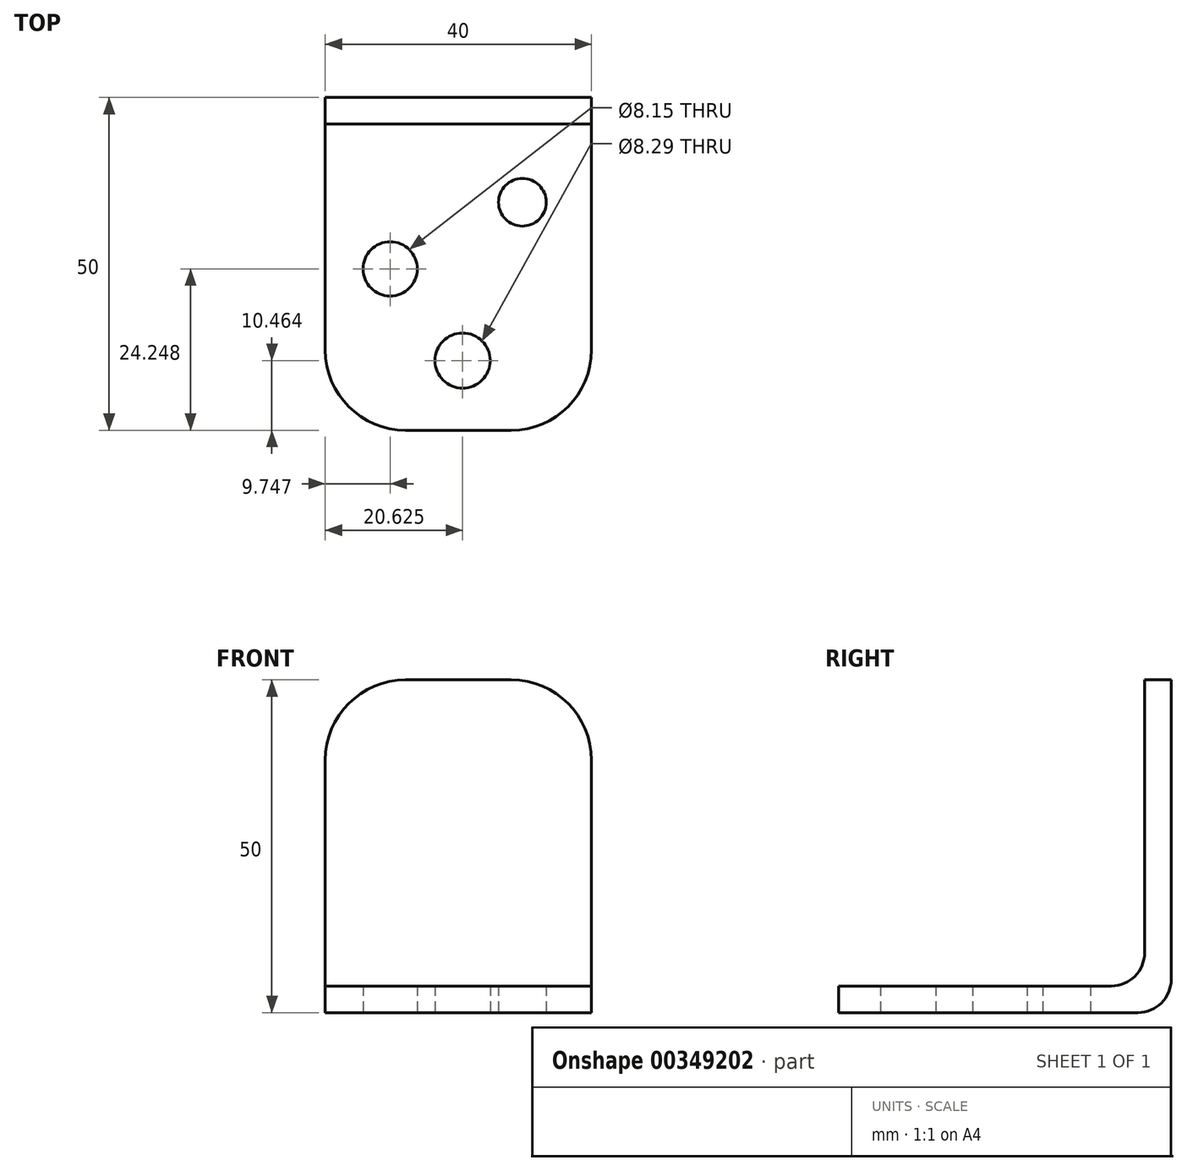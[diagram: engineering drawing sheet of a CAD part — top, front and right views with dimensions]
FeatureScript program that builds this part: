
annotation { "Feature Type Name" : "Feature", "Feature Type Description" : "" }
export const myFeature = defineFeature(function(context is Context, id is Id, definition is map)
    precondition{}
    {
        {
            var Q0;
            Q0=qCreatedBy(makeId("Front.planeOp"),FACE);
            var sketch = newSketch(context, id + "F0", { "sketchPlane" : qUnion([Q0])});
            skLineSegment(sketch, "E0.bottom", {"start": v(0, 0) * mm, "end": v(40, 0) * mm});
            skLineSegment(sketch, "E0.top", {"start": v(0, 50) * mm, "end": v(40, 50) * mm});
            skLineSegment(sketch, "E0.left", {"start": v(0, 0) * mm, "end": v(0, 50) * mm});
            skLineSegment(sketch, "E0.right", {"start": v(40, 0) * mm, "end": v(40, 50) * mm});
            skSolve(sketch);
        }
        {
            var Q0;
            Q0=makeQuery(id+"F0.imprint","IMPRINT",FACE,{"disambiguationData":[TD([[makeQuery(id+"F0.imprint","IMPRINT",EDGE,{"derivedFrom":sQuery(id+"F0.wireOp",EDGE,"E0.bottom")}),1.0]])]});
            extrude(context, id + "F1", {"entities" : qUnion([Q0]), "depth" : 4 * mm});
        }
        {
            var Q0;
            Q0=qCreatedBy(makeId("Top.planeOp"),FACE);
            var sketch = newSketch(context, id + "F2", { "sketchPlane" : qUnion([Q0])});
            skLineSegment(sketch, "E1.bottom", {"start": v(0, 0) * mm, "end": v(40, 0) * mm});
            skLineSegment(sketch, "E1.top", {"start": v(0, -50) * mm, "end": v(40, -50) * mm});
            skLineSegment(sketch, "E1.left", {"start": v(0, 0) * mm, "end": v(0, -50) * mm});
            skLineSegment(sketch, "E1.right", {"start": v(40, 0) * mm, "end": v(40, -50) * mm});
            skCircle(sketch, "E2", {"center": v(29.6, -15.74) * mm, "radius": 3.58 * mm});
            skCircle(sketch, "E3", {"center": v(9.75, -25.75) * mm, "radius": 4.08 * mm});
            skCircle(sketch, "E4", {"center": v(20.63, -39.54) * mm, "radius": 4.14 * mm});
            skSolve(sketch);
        }
        {
            var Q0;
            Q0=makeQuery(id+"F2.imprint","IMPRINT",FACE,{"disambiguationData":[TD([[makeQuery(id+"F2.imprint","IMPRINT",EDGE,{"derivedFrom":sQuery(id+"F2.wireOp",EDGE,"E1.bottom")}),-1.0]])]});
            extrude(context, id + "F3", {"entities" : qUnion([Q0]), "operationType" : NewBodyOperationType.ADD, "depth" : 4 * mm});
        }
        {
            var Q0;
            Q0=makeQuery(id+"F3.boolean.opBoolean","INTERSECT",EDGE,{"derivedFrom":[makeQuery(id+"F1.opExtrude","CAP_FACE",FACE,{"disambiguationData":[OSD([sQuery(id+"F0.wireOp",EDGE,"E0.bottom"),sQuery(id+"F0.wireOp",EDGE,"E0.top"),sQuery(id+"F0.wireOp",EDGE,"E0.left"),sQuery(id+"F0.wireOp",EDGE,"E0.right")])],"isStart":false}),makeQuery(id+"F3.opExtrude","CAP_FACE",FACE,{"disambiguationData":[OSD([sQuery(id+"F2.wireOp",EDGE,"E1.bottom"),sQuery(id+"F2.wireOp",EDGE,"E1.top"),sQuery(id+"F2.wireOp",EDGE,"E1.left"),sQuery(id+"F2.wireOp",EDGE,"E1.right"),sQuery(id+"F2.wireOp",EDGE,"E2"),sQuery(id+"F2.wireOp",EDGE,"E3"),sQuery(id+"F2.wireOp",EDGE,"E4")])],"isStart":false})]});
            fillet(context, id + "F4", {"entities" : qUnion([Q0]), "radius" : 5 * mm, "tangentPropagation" : true, "allowEdgeOverflow" : false});
        }
        {
            var Q0;
            Q0=makeQuery(id+"F1.opExtrude","CAP_EDGE",EDGE,{"disambiguationData":[OSD([sQuery(id+"F0.wireOp",EDGE,"E0.bottom")])],"isStart":true});
            fillet(context, id + "F5", {"entities" : qUnion([Q0]), "radius" : 5 * mm, "tangentPropagation" : true, "allowEdgeOverflow" : false});
        }
        {
            var Q0;
            Q0=makeQuery(id+"F3.opExtrude","SWEPT_EDGE",EDGE,{"disambiguationData":[OSD([sQuery(id+"F2.wireOp",EDGE,"E1.top"),sQuery(id+"F2.wireOp",EDGE,"E1.left")])]});
            var Q1;
            Q1=makeQuery(id+"F3.opExtrude","SWEPT_EDGE",EDGE,{"disambiguationData":[OSD([sQuery(id+"F2.wireOp",EDGE,"E1.top"),sQuery(id+"F2.wireOp",EDGE,"E1.right")])]});
            var Q2;
            Q2=makeQuery(id+"F1.opExtrude","SWEPT_EDGE",EDGE,{"disambiguationData":[OSD([sQuery(id+"F0.wireOp",EDGE,"E0.top"),sQuery(id+"F0.wireOp",EDGE,"E0.right")])]});
            var Q3;
            Q3=makeQuery(id+"F1.opExtrude","SWEPT_EDGE",EDGE,{"disambiguationData":[OSD([sQuery(id+"F0.wireOp",EDGE,"E0.top"),sQuery(id+"F0.wireOp",EDGE,"E0.left")])]});
            fillet(context, id + "F6", {"entities" : qUnion([Q0, Q1, Q2, Q3]), "radius" : 12.07 * mm, "tangentPropagation" : true, "allowEdgeOverflow" : false});
        }
    });
